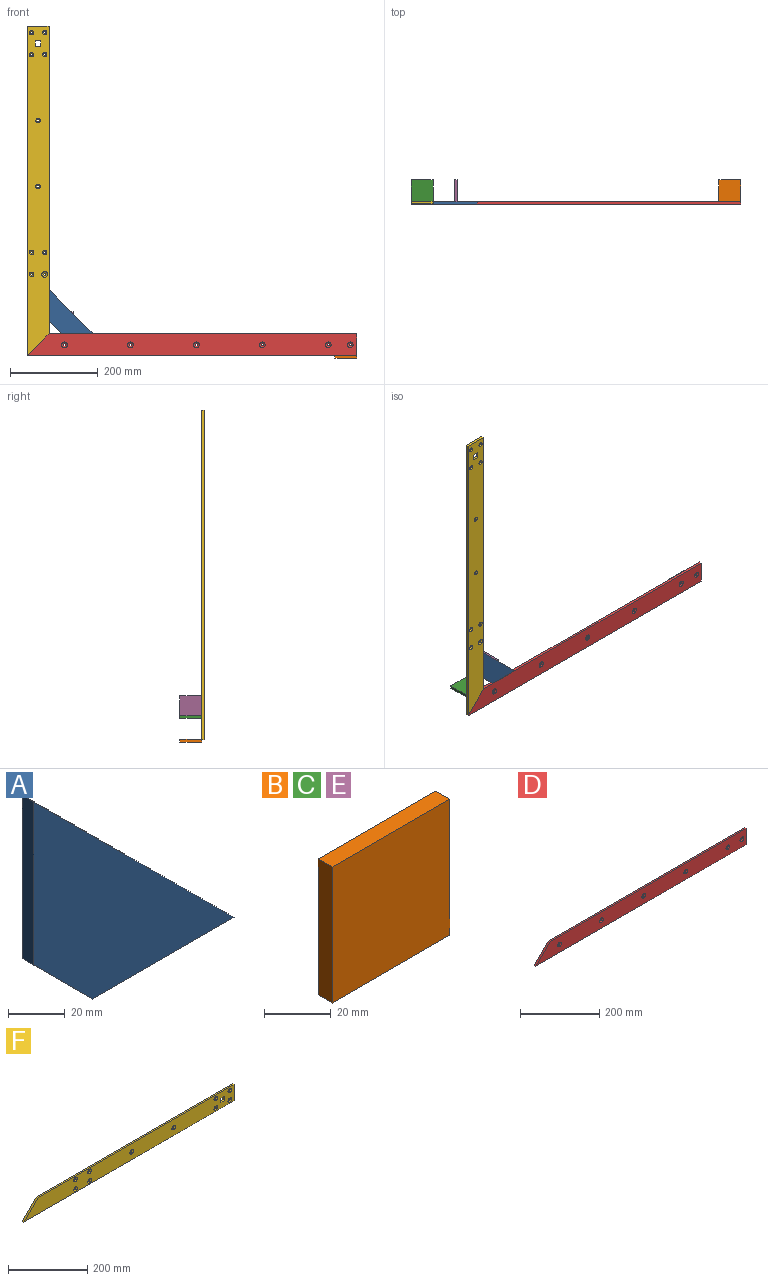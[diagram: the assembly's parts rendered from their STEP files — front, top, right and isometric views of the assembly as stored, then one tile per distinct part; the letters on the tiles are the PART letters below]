
ASSEMBLY  parts=6 mates=5
PART A: 6 faces, bbox 100x6x100 mm
  f0: plane 100x100mm, normal (0.71,0,0.71), area 848.5mm2, adj f1,f3,f4,f5
  f1: plane 70.71x6mm, normal (-1,0,0), area 424.3mm2, adj f0,f2,f4,f5
  f2: plane 29.29x29.29mm, normal (-0.71,0,-0.71), area 248.5mm2, adj f1,f3,f4,f5
  f3: plane 70.71x6mm, normal (0,0,-1), area 424.3mm2, adj f0,f2,f4,f5
  f4: plane 100x100mm, normal (0,-1,0), area 4571.1mm2, adj f0,f1,f2,f3
  f5: plane 100x100mm, normal (0,1,0), area 4571.1mm2, adj f0,f1,f2,f3
PART B: 6 faces, bbox 50x6x50 mm
  f0: plane 50x6mm, normal (1,0,0), area 300mm2, adj f1,f3,f4,f5
  f1: plane 50x6mm, normal (0,0,1), area 300mm2, adj f0,f2,f4,f5
  f2: plane 50x6mm, normal (-1,0,0), area 300mm2, adj f1,f3,f4,f5
  f3: plane 50x6mm, normal (0,0,-1), area 300mm2, adj f0,f2,f4,f5
  f4: plane 50x50mm, normal (0,-1,0), area 2500mm2, adj f0,f1,f2,f3
  f5: plane 50x50mm, normal (0,1,0), area 2500mm2, adj f0,f1,f2,f3
PART C: same geometry as B
PART D: 24 faces, bbox 750x6x50 mm
  f0: plane 50x6mm, normal (1,0,0), area 300mm2, adj f1,f8,f10,f11
  f1: plane 700x6mm, normal (0,0,1), area 4200mm2, adj f0,f2,f10,f11
  f2: plane 50x50mm, normal (-0.71,0,0.71), area 424.3mm2, adj f1,f8,f10,f11
  f3: cylinder r=3mm len=6mm, axis (0,1,0), area 10.1mm2, adj f18,f19
  f4: cylinder r=3mm len=6mm, axis (0,1,0), area 10.1mm2, adj f14,f15
  f5: cylinder r=3mm len=6mm, axis (0,1,0), area 10.1mm2, adj f12,f13
  f6: cylinder r=3mm len=6mm, axis (0,1,0), area 37.7mm2, adj f22,f23
  f7: cylinder r=3mm len=6mm, axis (0,1,0), area 10.1mm2, adj f20,f21
  f8: plane 750x6mm, normal (0,0,-1), area 4500mm2, adj f0,f2,f10,f11
  f9: cylinder r=3mm len=6mm, axis (0,1,0), area 10.1mm2, adj f16,f17
  f10: plane 750x50mm, normal (0,-1,0), area 35462.4mm2, adj f0,f1,f2,f8,f12,f14,f16,f18
  f11: plane 750x50mm, normal (0,1,0), area 35726mm2, adj f0,f1,f2,f8,f13,f15,f17,f19
  f12: cone r=3mm half-angle=60deg, axis (0,-1,0), area 118.9mm2, adj f5,f10
  f13: cone r=5mm half-angle=30deg, axis (0,1,0), area 100.5mm2, adj f5,f11
  f14: cone r=3mm half-angle=60deg, axis (0,-1,0), area 118.9mm2, adj f4,f10
  f15: cone r=5mm half-angle=30deg, axis (0,1,0), area 100.5mm2, adj f4,f11
  f16: cone r=3mm half-angle=60deg, axis (0,-1,0), area 118.9mm2, adj f9,f10
  f17: cone r=5mm half-angle=30deg, axis (0,1,0), area 100.5mm2, adj f9,f11
  f18: cone r=3mm half-angle=60deg, axis (0,-1,0), area 118.9mm2, adj f3,f10
  f19: cone r=5mm half-angle=30deg, axis (0,1,0), area 100.5mm2, adj f3,f11
  f20: cone r=5mm half-angle=30deg, axis (0,1,0), area 100.5mm2, adj f7,f11
  f21: cone r=3mm half-angle=60deg, axis (0,-1,0), area 118.9mm2, adj f7,f10
  f22: cone r=6.46mm half-angle=60deg, axis (0,1,0), area 118.9mm2, adj f6,f11
  f23: cone r=3mm half-angle=60deg, axis (0,-1,0), area 118.9mm2, adj f6,f10
PART E: same geometry as B
PART F: 40 faces, bbox 750x6x50 mm
  f0: plane 13x6mm, normal (0,0,-1), area 78mm2, adj f1,f17,f18,f19
  f1: plane 13x6mm, normal (-1,0,0), area 78mm2, adj f0,f2,f18,f19
  f2: plane 13x6mm, normal (0,0,1), area 78mm2, adj f1,f17,f18,f19
  f3: plane 50x6mm, normal (1,0,0), area 300mm2, adj f4,f16,f18,f19
  f4: plane 700x6mm, normal (0,0,1), area 4200mm2, adj f3,f5,f18,f19
  f5: plane 50x50mm, normal (-0.71,0,0.71), area 424.3mm2, adj f4,f16,f18,f19
  f6: cylinder r=3mm len=6mm, axis (0,1,0), area 10.1mm2, adj f25,f34
  f7: cylinder r=3mm len=6mm, axis (0,1,0), area 10.1mm2, adj f24,f35
  f8: cylinder r=3mm len=6mm, axis (0,1,0), area 10.1mm2, adj f21,f37
  f9: cylinder r=3mm len=6mm, axis (0,1,0), area 37.7mm2, adj f20,f39
  f10: cylinder r=3mm len=6mm, axis (0,1,0), area 10.1mm2, adj f23,f36
  f11: cylinder r=3mm len=6mm, axis (0,1,0), area 10.1mm2, adj f22,f38
  f12: cylinder r=3mm len=6mm, axis (0,1,0), area 10.1mm2, adj f28,f32
  f13: cylinder r=3mm len=6mm, axis (0,1,0), area 10.1mm2, adj f26,f33
  f14: cylinder r=3mm len=6mm, axis (0,1,0), area 10.1mm2, adj f29,f30
  f15: cylinder r=3mm len=6mm, axis (0,1,0), area 10.1mm2, adj f27,f31
  f16: plane 750x6mm, normal (0,0,-1), area 4500mm2, adj f3,f5,f18,f19
  f17: plane 13x6mm, normal (1,0,0), area 78mm2, adj f0,f2,f18,f19
  f18: plane 750x50mm, normal (0,-1,0), area 34768.3mm2, adj f0,f1,f2,f3,f4,f5,f16,f17
  f19: plane 750x50mm, normal (0,1,0), area 35242.9mm2, adj f0,f1,f2,f3,f4,f5,f16,f17
  f20: cone r=6.46mm half-angle=60deg, axis (0,1,0), area 118.9mm2, adj f9,f19
  f21: cone r=5mm half-angle=30deg, axis (0,1,0), area 100.5mm2, adj f8,f19
  f22: cone r=5mm half-angle=30deg, axis (0,1,0), area 100.5mm2, adj f11,f19
  f23: cone r=5mm half-angle=30deg, axis (0,1,0), area 100.5mm2, adj f10,f19
  f24: cone r=5mm half-angle=30deg, axis (0,1,0), area 100.5mm2, adj f7,f19
  f25: cone r=5mm half-angle=30deg, axis (0,1,0), area 100.5mm2, adj f6,f19
  f26: cone r=5mm half-angle=30deg, axis (0,1,0), area 100.5mm2, adj f13,f19
  f27: cone r=5mm half-angle=30deg, axis (0,1,0), area 100.5mm2, adj f15,f19
  f28: cone r=5mm half-angle=30deg, axis (0,1,0), area 100.5mm2, adj f12,f19
  f29: cone r=5mm half-angle=30deg, axis (0,1,0), area 100.5mm2, adj f14,f19
  f30: cone r=3mm half-angle=60deg, axis (0,-1,0), area 118.9mm2, adj f14,f18
  f31: cone r=3mm half-angle=60deg, axis (0,-1,0), area 118.9mm2, adj f15,f18
  f32: cone r=3mm half-angle=60deg, axis (0,-1,0), area 118.9mm2, adj f12,f18
  f33: cone r=3mm half-angle=60deg, axis (0,-1,0), area 118.9mm2, adj f13,f18
  f34: cone r=3mm half-angle=60deg, axis (0,-1,0), area 118.9mm2, adj f6,f18
  f35: cone r=3mm half-angle=60deg, axis (0,-1,0), area 118.9mm2, adj f7,f18
  f36: cone r=3mm half-angle=60deg, axis (0,-1,0), area 118.9mm2, adj f10,f18
  f37: cone r=3mm half-angle=60deg, axis (0,-1,0), area 118.9mm2, adj f8,f18
  f38: cone r=3mm half-angle=60deg, axis (0,-1,0), area 118.9mm2, adj f11,f18
  f39: cone r=3mm half-angle=60deg, axis (0,-1,0), area 118.9mm2, adj f9,f18
PLACE A t=(-280.33,-2.08,-223.3)mm
PLACE B rot(axis=(-1,0,0),90deg) t=(344.67,25.92,-325.3)mm
PLACE C rot(axis=(0,0.71,0.71),180deg) t=(-355.33,25.92,-271.3)mm
PLACE D t=(-5.33,-2.08,-298.3)mm fixed
PLACE E rot(axis=(-0.58,0.58,0.58),120deg) t=(-278.33,25.92,-248.3)mm
PLACE F rot(axis=(0.71,0,0.71),180deg) t=(-355.33,-2.08,51.7)mm
MATE fastened A.f1 <-> F.f4  axis (-1,0,0) through (-330.33,-2.08,-173.3)mm
MATE fastened F.f5 <-> D.f2  axis (0.71,0,-0.71) through (-355.33,-2.08,-298.3)mm
MATE fastened C.f3 <-> F.f18  axis (0,-1,0) through (-355.33,0.92,-274.3)mm
MATE fastened B.f3 <-> D.f11  axis (0,-1,0) through (344.67,0.92,-322.3)mm
MATE fastened E.f3 <-> F.f18  axis (0,-1,0) through (-281.33,0.92,-273.3)mm
